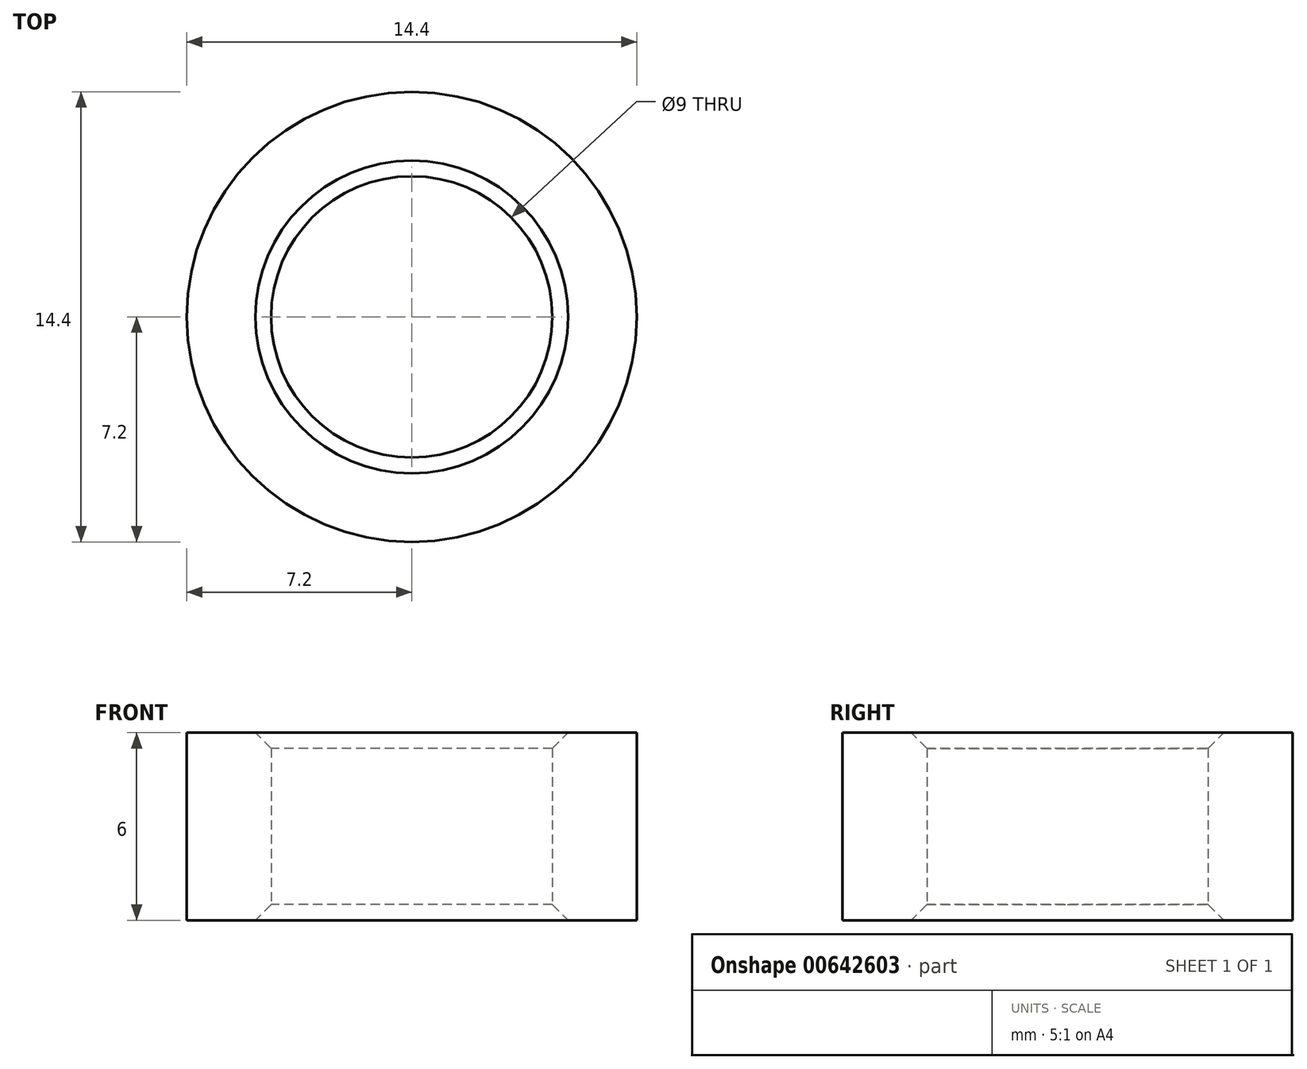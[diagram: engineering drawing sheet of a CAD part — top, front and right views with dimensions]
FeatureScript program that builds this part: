
annotation { "Feature Type Name" : "Feature", "Feature Type Description" : "" }
export const myFeature = defineFeature(function(context is Context, id is Id, definition is map)
    precondition{}
    {
        {
            var Q0;
            Q0=qCreatedBy(makeId("Top.planeOp"),FACE);
            var sketch = newSketch(context, id + "F0", { "sketchPlane" : qUnion([Q0])});
            skCircle(sketch, "E0", {"center": v(0, 0) * mm, "radius": 7.2 * mm});
            skCircle(sketch, "E1", {"center": v(0, 0) * mm, "radius": 4.5 * mm});
            skSolve(sketch);
        }
        {
            var Q0;
            Q0=makeQuery(id+"F0.imprint","IMPRINT",FACE,{"disambiguationData":[TD([[makeQuery(id+"F0.imprint","IMPRINT",EDGE,{"derivedFrom":sQuery(id+"F0.wireOp",EDGE,"E0")}),1.0]])]});
            extrude(context, id + "F1", {"entities" : qUnion([Q0]), "depth" : 6 * mm, "offsetDistance" : 25 * mm});
        }
        {
            var Q0;
            Q0=makeQuery(id+"F1.opExtrude","CAP_EDGE",EDGE,{"disambiguationData":[OSD([sQuery(id+"F0.wireOp",EDGE,"E1")])],"isStart":false});
            var Q1;
            Q1=makeQuery(id+"F1.opExtrude","CAP_EDGE",EDGE,{"disambiguationData":[OSD([sQuery(id+"F0.wireOp",EDGE,"E1")])],"isStart":true});
            chamfer(context, id + "F2", {"entities" : qUnion([Q0, Q1]), "chamferType" : ChamferType.OFFSET_ANGLE, "width" : 0.5 * mm, "oppositeDirection" : false, "angle" : 45 * degree, "tangentPropagation" : true});
        }
    });
